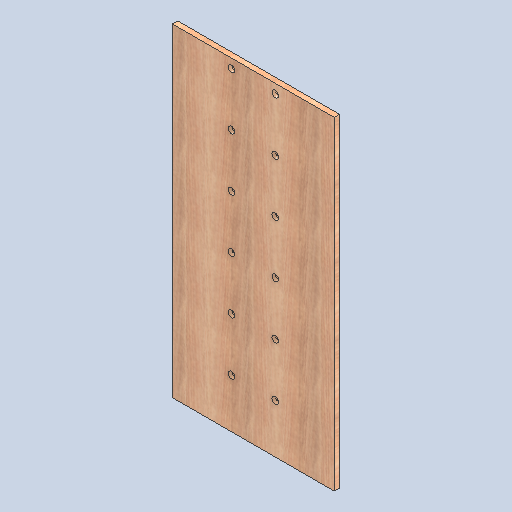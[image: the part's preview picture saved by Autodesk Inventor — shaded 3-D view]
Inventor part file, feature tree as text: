
AUTODESK INVENTOR PART (.ipt)
format: ipt  version: 2022 (Build 260153000, 153)  size: 275,456 bytes
history: native  units: mm
features: sketch x4, extrude x3, other x3, reference x2, projected_geometry x2, hole x1, mirror x1, pattern_linear x1
ambient origin geometry x8: Origin, YZ Plane, XZ Plane, XY Plane, X Axis, Y Axis, Z Axis, Center Point
bodies: Solid1 (feature_tree)
feature tree (17):
  extrude  "Extrusion1"  Depth=1220.0mm
  extrude  "Extrusion2"  TaperAngle=0.0deg  [1 undecoded]
  hole  "Hole1"  [1 undecoded]
  mirror  "Mirror1"
  pattern_linear  "Rectangular Pattern1"  [2 undecoded]
  extrude  "Extrusion3"  [1 undecoded]
  sketch  "Sketch1"  dims[d0=610.0mm d1=1220.0mm]
  sketch  "Sketch2"  dims[d2=20.0mm d3=0.0mm d4=0.0mm d5=0.0mm]
  reference  "Reference1"
  reference  "Reference2"
  sketch  "Sketch3"  dims[d6=8.0mm d7=20.0mm d8=25.0mm d9=2.0mm d10=90.0deg d11=27.3mm d12=20.594885mm d13=60.0mm d15=200.0mm]
  sketch  "Sketch4"  dims[d16=0.0mm d17=0.0mm]
  projected_geometry  "Projected Loop1"
  projected_geometry  "Projected Loop2"
  other  "IMS-00-000.iam"
  other  "IMS-10-000:1"
  other  "IMS-10-001:1"
note: 5 required parameter values undecoded (feature->parameter linkage not recoverable at this tier; creation-order binding heuristic only, values carry confidence <= 0.55)
